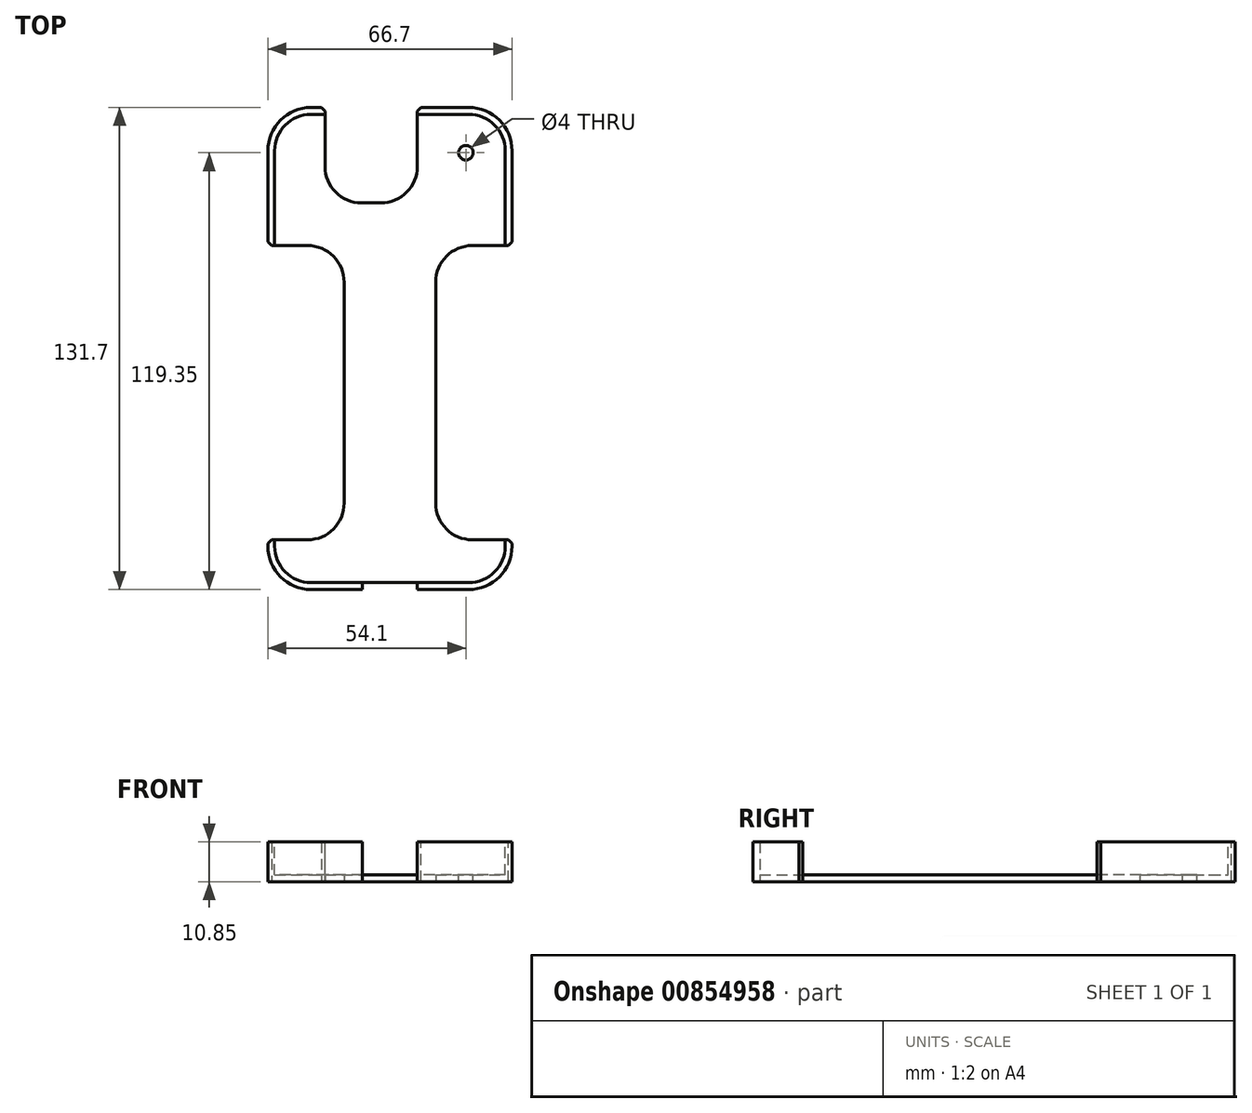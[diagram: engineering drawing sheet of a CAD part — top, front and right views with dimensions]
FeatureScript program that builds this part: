
annotation { "Feature Type Name" : "Feature", "Feature Type Description" : "" }
export const myFeature = defineFeature(function(context is Context, id is Id, definition is map)
    precondition{}
    {
        {
            assignVariable(context, id + "F0", {"name" : "wallThickness", "anyValue" : 1.85 * mm});
        }
        {
            var Q0;
            Q0=qCreatedBy(makeId("Top.planeOp"),FACE);
            var sketch = newSketch(context, id + "F1", { "sketchPlane" : qUnion([Q0])});
            skLineSegment(sketch, "E0.bottom", {"start": v(0.75, 10.5) * mm, "end": v(-42.25, 10.5) * mm});
            skLineSegment(sketch, "E0.top", {"start": v(0.75, -117.5) * mm, "end": v(-42.25, -117.5) * mm});
            skLineSegment(sketch, "E0.left", {"start": v(10.75, 0.5) * mm, "end": v(10.75, -107.5) * mm});
            skLineSegment(sketch, "E0.right", {"start": v(-52.25, 0.5) * mm, "end": v(-52.25, -107.5) * mm});
            skLineSegment(sketch, "E1", {"start": v(-20.75, 10.5) * mm, "end": v(-20.75, -117.5) * mm, "construction": true});
            skLineSegment(sketch, "E2", {"start": v(-13.25, 16.06) * mm, "end": v(-13.25, -123.66) * mm, "construction": true});
            skLineSegment(sketch, "E3", {"start": v(-28.25, 15.98) * mm, "end": v(-28.25, -123.54) * mm, "construction": true});
            skLineSegment(sketch, "E4", {"start": v(10.75, -53.5) * mm, "end": v(-52.25, -53.5) * mm, "construction": true});
            skLineSegment(sketch, "E5", {"start": v(-1.25, 14.38) * mm, "end": v(-1.25, -123.66) * mm, "construction": true});
            skLineSegment(sketch, "E6", {"start": v(-13.25, -123.66) * mm, "end": v(10.75, -123.66) * mm, "construction": true});
            skPoint(sketch, "E7.visualSharp", {"position": v(-52.25, 10.5) * mm});
            skArc(sketch, "E7.filletArc", {"start": v(-42.25, 10.5) * mm, "mid": v(-49.32, 7.57) * mm, "end": v(-52.25, 0.5) * mm});
            skPoint(sketch, "E8.visualSharp", {"position": v(10.75, 10.5) * mm});
            skArc(sketch, "E8.filletArc", {"start": v(10.75, 0.5) * mm, "mid": v(7.82, 7.57) * mm, "end": v(0.75, 10.5) * mm});
            skPoint(sketch, "E9.visualSharp", {"position": v(10.75, -117.5) * mm});
            skArc(sketch, "E9.filletArc", {"start": v(0.75, -117.5) * mm, "mid": v(7.82, -114.57) * mm, "end": v(10.75, -107.5) * mm});
            skPoint(sketch, "E10.visualSharp", {"position": v(-52.25, -117.5) * mm});
            skArc(sketch, "E10.filletArc", {"start": v(-52.25, -107.5) * mm, "mid": v(-49.32, -114.57) * mm, "end": v(-42.25, -117.5) * mm});
            skLineSegment(sketch, "E11.bottom", {"start": v(-42.25, 12.35) * mm, "end": v(0.75, 12.35) * mm});
            skLineSegment(sketch, "E11.top", {"start": v(-42.25, -119.35) * mm, "end": v(0.75, -119.35) * mm});
            skLineSegment(sketch, "E11.left", {"start": v(-54.1, 0.5) * mm, "end": v(-54.1, -107.5) * mm});
            skLineSegment(sketch, "E11.right", {"start": v(12.6, 0.5) * mm, "end": v(12.6, -107.5) * mm});
            skPoint(sketch, "E12.visualSharp", {"position": v(-54.1, -119.35) * mm});
            skArc(sketch, "E12.filletArc", {"start": v(-54.1, -107.5) * mm, "mid": v(-50.63, -115.88) * mm, "end": v(-42.25, -119.35) * mm});
            skPoint(sketch, "E13.visualSharp", {"position": v(12.6, -119.35) * mm});
            skArc(sketch, "E13.filletArc", {"start": v(0.75, -119.35) * mm, "mid": v(9.13, -115.88) * mm, "end": v(12.6, -107.5) * mm});
            skPoint(sketch, "E14.visualSharp", {"position": v(12.6, 12.35) * mm});
            skArc(sketch, "E14.filletArc", {"start": v(12.6, 0.5) * mm, "mid": v(9.13, 8.88) * mm, "end": v(0.75, 12.35) * mm});
            skPoint(sketch, "E15.visualSharp", {"position": v(-54.1, 12.35) * mm});
            skArc(sketch, "E15.filletArc", {"start": v(-42.25, 12.35) * mm, "mid": v(-50.63, 8.88) * mm, "end": v(-54.1, 0.5) * mm});
            skCircle(sketch, "E16", {"center": v(0, 0) * mm, "radius": 2 * mm});
            skSolve(sketch);
        }
        {
            var Q0;
            Q0=sQuery(id+"F1.wireOp",EDGE,"E0.left");
            cPlane(context, id + "F2", {"entities" : qUnion([Q0]), "cplaneType" : CPlaneType.MID_PLANE, "offset" : 25 * mm, "width" : 150 * mm, "height" : 150 * mm});
        }
        {
            var Q0;
            Q0=qCreatedBy(id+"F2.planeOp",FACE);
            var sketch = newSketch(context, id + "F3", { "sketchPlane" : qUnion([Q0])});
            skLineSegment(sketch, "E17.bottom", {"start": v(10.75, 9) * mm, "end": v(12.6, 9) * mm});
            skLineSegment(sketch, "E17.top", {"start": v(10.75, 0) * mm, "end": v(12.6, 0) * mm});
            skLineSegment(sketch, "E17.left", {"start": v(10.75, 9) * mm, "end": v(10.75, 0) * mm});
            skLineSegment(sketch, "E17.right", {"start": v(12.6, 9) * mm, "end": v(12.6, 0) * mm});
            skSolve(sketch);
        }
        {
            var Q0;
            Q0=makeQuery(id+"F3.imprint","IMPRINT",FACE,{"disambiguationData":[TD([[makeQuery(id+"F3.imprint","IMPRINT",EDGE,{"derivedFrom":sQuery(id+"F3.wireOp",EDGE,"E17.bottom")}),-1.0]])]});
            var Q1;
            Q1=sQuery(id+"F1.wireOp",EDGE,"E0.left");
            var Q2;
            Q2=sQuery(id+"F1.wireOp",EDGE,"E8.filletArc");
            var Q3;
            Q3=sQuery(id+"F1.wireOp",EDGE,"E9.filletArc");
            var Q4;
            Q4=sQuery(id+"F1.wireOp",EDGE,"E0.top");
            var Q5;
            Q5=sQuery(id+"F1.wireOp",EDGE,"E10.filletArc");
            var Q6;
            Q6=sQuery(id+"F1.wireOp",EDGE,"E0.bottom");
            var Q7;
            Q7=sQuery(id+"F1.wireOp",EDGE,"E7.filletArc");
            var Q8;
            Q8=sQuery(id+"F1.wireOp",EDGE,"E0.right");
            sweep(context, id + "F4", {"profiles" : qUnion([Q0]), "path" : qUnion([Q1, Q2, Q3, Q4, Q5, Q6, Q7, Q8])});
        }
        {
            var Q0;
            Q0=makeQuery(id+"F1.imprint","IMPRINT",FACE,{"disambiguationData":[TD([[makeQuery(id+"F1.imprint","IMPRINT",EDGE,{"derivedFrom":sQuery(id+"F1.wireOp",EDGE,"E0.bottom")}),1.0]])]});
            var Q1;
            Q1=makeQuery(id+"F1.imprint","IMPRINT",FACE,{"disambiguationData":[TD([[makeQuery(id+"F1.imprint","IMPRINT",EDGE,{"derivedFrom":sQuery(id+"F1.wireOp",EDGE,"E0.bottom")}),-1.0]])]});
            extrude(context, id + "F5", {"entities" : qUnion([Q0, Q1]), "operationType" : NewBodyOperationType.ADD, "oppositeDirection" : true, "depth" : getVariable(context, 'wallThickness'), "offsetDistance" : 25 * mm});
        }
        {
            var Q0;
            Q0=qCreatedBy(makeId("Top.planeOp"),FACE);
            var sketch = newSketch(context, id + "F6", { "sketchPlane" : qUnion([Q0])});
            skLineSegment(sketch, "E18.bottom", {"start": v(-38.5, 18) * mm, "end": v(-13.25, 18) * mm});
            skLineSegment(sketch, "E18.top", {"start": v(-38.5, -13.74) * mm, "end": v(-13.25, -13.74) * mm});
            skLineSegment(sketch, "E18.left", {"start": v(-38.5, 18) * mm, "end": v(-38.5, -13.74) * mm});
            skLineSegment(sketch, "E18.right", {"start": v(-13.25, 18) * mm, "end": v(-13.25, -13.74) * mm});
            skLineSegment(sketch, "E19.bottom", {"start": v(-28.25, -135.17) * mm, "end": v(-13.25, -135.17) * mm});
            skLineSegment(sketch, "E19.top", {"start": v(-28.25, -117.5) * mm, "end": v(-13.25, -117.5) * mm});
            skLineSegment(sketch, "E19.left", {"start": v(-28.25, -135.17) * mm, "end": v(-28.25, -117.5) * mm});
            skLineSegment(sketch, "E19.right", {"start": v(-13.25, -135.17) * mm, "end": v(-13.25, -117.5) * mm});
            skLineSegment(sketch, "E20.bottom", {"start": v(-65.33, -25.38) * mm, "end": v(-33.25, -25.38) * mm});
            skLineSegment(sketch, "E20.top", {"start": v(-65.33, -105.77) * mm, "end": v(-33.25, -105.77) * mm});
            skLineSegment(sketch, "E20.left", {"start": v(-65.33, -25.38) * mm, "end": v(-65.33, -105.77) * mm});
            skLineSegment(sketch, "E20.right", {"start": v(-33.25, -25.38) * mm, "end": v(-33.25, -105.77) * mm});
            skLineSegment(sketch, "E21.bottom", {"start": v(22.57, -25.38) * mm, "end": v(-8.25, -25.38) * mm});
            skLineSegment(sketch, "E21.top", {"start": v(22.57, -105.77) * mm, "end": v(-8.25, -105.77) * mm});
            skLineSegment(sketch, "E21.left", {"start": v(22.57, -25.38) * mm, "end": v(22.57, -105.77) * mm});
            skLineSegment(sketch, "E21.right", {"start": v(-8.25, -25.38) * mm, "end": v(-8.25, -105.77) * mm});
            skSolve(sketch);
        }
        {
            var Q0;
            Q0 = qSketchRegion(id + "F6", true);
            extrude(context, id + "F7", {"entities" : qUnion([Q0]), "operationType" : NewBodyOperationType.REMOVE, "endBound" : BoundingType.SYMMETRIC, "depth" : 50 * mm, "offsetDistance" : 25 * mm});
        }
        {
            var Q0;
            Q0=makeQuery(id+"F7.boolean.opBoolean","COPY",EDGE,{"derivedFrom":makeQuery(id+"F7.opExtrude","SWEPT_EDGE",EDGE,{"disambiguationData":[OSD([sQuery(id+"F6.wireOp",EDGE,"E20.bottom"),sQuery(id+"F6.wireOp",EDGE,"E20.right")])]})});
            var Q1;
            Q1=makeQuery(id+"F7.boolean.opBoolean","COPY",EDGE,{"derivedFrom":makeQuery(id+"F7.opExtrude","SWEPT_EDGE",EDGE,{"disambiguationData":[OSD([sQuery(id+"F6.wireOp",EDGE,"E21.bottom"),sQuery(id+"F6.wireOp",EDGE,"E21.right")])]})});
            var Q2;
            Q2=makeQuery(id+"F7.boolean.opBoolean","COPY",EDGE,{"derivedFrom":makeQuery(id+"F7.opExtrude","SWEPT_EDGE",EDGE,{"disambiguationData":[OSD([sQuery(id+"F6.wireOp",EDGE,"E21.top"),sQuery(id+"F6.wireOp",EDGE,"E21.right")])]})});
            var Q3;
            Q3=makeQuery(id+"F7.boolean.opBoolean","COPY",EDGE,{"derivedFrom":makeQuery(id+"F7.opExtrude","SWEPT_EDGE",EDGE,{"disambiguationData":[OSD([sQuery(id+"F6.wireOp",EDGE,"E20.top"),sQuery(id+"F6.wireOp",EDGE,"E20.right")])]})});
            var Q4;
            Q4=makeQuery(id+"F7.boolean.opBoolean","COPY",EDGE,{"derivedFrom":makeQuery(id+"F7.opExtrude","SWEPT_EDGE",EDGE,{"disambiguationData":[OSD([sQuery(id+"F6.wireOp",EDGE,"E18.top"),sQuery(id+"F6.wireOp",EDGE,"E18.left")])]})});
            var Q5;
            Q5=makeQuery(id+"F7.boolean.opBoolean","COPY",EDGE,{"derivedFrom":makeQuery(id+"F7.opExtrude","SWEPT_EDGE",EDGE,{"disambiguationData":[OSD([sQuery(id+"F6.wireOp",EDGE,"E18.top"),sQuery(id+"F6.wireOp",EDGE,"E18.right")])]})});
            fillet(context, id + "F8", {"entities" : qUnion([Q0, Q1, Q2, Q3, Q4, Q5]), "radius" : 10 * mm, "tangentPropagation" : true, "allowEdgeOverflow" : false});
        }
        {
            var Q0;
            Q0=makeQuery(id+"F7.boolean.opBoolean","INTERSECT",EDGE,{"derivedFrom":[makeQuery(id+"F5.boolean.opBoolean","MERGE",FACE,{"derivedFrom":[makeQuery(id+"F4.opSweep","SWEPT_FACE",FACE,{"disambiguationData":[OSD([sQuery(id+"F1.wireOp",EDGE,"E0.right"),sQuery(id+"F3.wireOp",EDGE,"E17.right")])]}),makeQuery(id+"F5.opExtrude","SWEPT_FACE",FACE,{"disambiguationData":[OSD([sQuery(id+"F1.wireOp",EDGE,"E11.left")])]})]}),makeQuery(id+"F7.opExtrude","SWEPT_FACE",FACE,{"disambiguationData":[OSD([sQuery(id+"F6.wireOp",EDGE,"E20.bottom")])]})]});
            var Q1;
            Q1=makeQuery(id+"F7.boolean.opBoolean","INTERSECT",EDGE,{"derivedFrom":[makeQuery(id+"F5.boolean.opBoolean","MERGE",FACE,{"derivedFrom":[makeQuery(id+"F4.opSweep","SWEPT_FACE",FACE,{"disambiguationData":[OSD([sQuery(id+"F1.wireOp",EDGE,"E0.left"),sQuery(id+"F3.wireOp",EDGE,"E17.right")])]}),makeQuery(id+"F5.opExtrude","SWEPT_FACE",FACE,{"disambiguationData":[OSD([sQuery(id+"F1.wireOp",EDGE,"E11.right")])]})]}),makeQuery(id+"F7.opExtrude","SWEPT_FACE",FACE,{"disambiguationData":[OSD([sQuery(id+"F6.wireOp",EDGE,"E21.bottom")])]})]});
            var Q2;
            Q2=makeQuery(id+"F7.boolean.opBoolean","INTERSECT",EDGE,{"derivedFrom":[makeQuery(id+"F5.boolean.opBoolean","MERGE",FACE,{"derivedFrom":[makeQuery(id+"F4.opSweep","SWEPT_FACE",FACE,{"disambiguationData":[OSD([sQuery(id+"F1.wireOp",EDGE,"E0.bottom"),sQuery(id+"F3.wireOp",EDGE,"E17.right")])]}),makeQuery(id+"F5.opExtrude","SWEPT_FACE",FACE,{"disambiguationData":[OSD([sQuery(id+"F1.wireOp",EDGE,"E11.bottom")])]})]}),makeQuery(id+"F7.opExtrude","SWEPT_FACE",FACE,{"disambiguationData":[OSD([sQuery(id+"F6.wireOp",EDGE,"E18.right")])]})]});
            var Q3;
            Q3=makeQuery(id+"F7.boolean.opBoolean","INTERSECT",EDGE,{"derivedFrom":[makeQuery(id+"F5.boolean.opBoolean","MERGE",FACE,{"derivedFrom":[makeQuery(id+"F4.opSweep","SWEPT_FACE",FACE,{"disambiguationData":[OSD([sQuery(id+"F1.wireOp",EDGE,"E0.bottom"),sQuery(id+"F3.wireOp",EDGE,"E17.right")])]}),makeQuery(id+"F5.opExtrude","SWEPT_FACE",FACE,{"disambiguationData":[OSD([sQuery(id+"F1.wireOp",EDGE,"E11.bottom")])]})]}),makeQuery(id+"F7.opExtrude","SWEPT_FACE",FACE,{"disambiguationData":[OSD([sQuery(id+"F6.wireOp",EDGE,"E18.left")])]})]});
            var Q4;
            Q4=makeQuery(id+"F7.boolean.opBoolean","INTERSECT",EDGE,{"derivedFrom":[makeQuery(id+"F5.boolean.opBoolean","MERGE",FACE,{"derivedFrom":[makeQuery(id+"F4.opSweep","SWEPT_FACE",FACE,{"disambiguationData":[OSD([sQuery(id+"F1.wireOp",EDGE,"E0.right"),sQuery(id+"F3.wireOp",EDGE,"E17.right")])]}),makeQuery(id+"F5.opExtrude","SWEPT_FACE",FACE,{"disambiguationData":[OSD([sQuery(id+"F1.wireOp",EDGE,"E11.left")])]})]}),makeQuery(id+"F7.opExtrude","SWEPT_FACE",FACE,{"disambiguationData":[OSD([sQuery(id+"F6.wireOp",EDGE,"E20.top")])]})]});
            var Q5;
            Q5=makeQuery(id+"F7.boolean.opBoolean","INTERSECT",EDGE,{"derivedFrom":[makeQuery(id+"F5.boolean.opBoolean","MERGE",FACE,{"derivedFrom":[makeQuery(id+"F4.opSweep","SWEPT_FACE",FACE,{"disambiguationData":[OSD([sQuery(id+"F1.wireOp",EDGE,"E0.left"),sQuery(id+"F3.wireOp",EDGE,"E17.right")])]}),makeQuery(id+"F5.opExtrude","SWEPT_FACE",FACE,{"disambiguationData":[OSD([sQuery(id+"F1.wireOp",EDGE,"E11.right")])]})]}),makeQuery(id+"F7.opExtrude","SWEPT_FACE",FACE,{"disambiguationData":[OSD([sQuery(id+"F6.wireOp",EDGE,"E21.top")])]})]});
            chamfer(context, id + "F9", {"entities" : qUnion([Q0, Q1, Q2, Q3, Q4, Q5]), "width" : 1 * mm, "tangentPropagation" : true});
        }
    });
